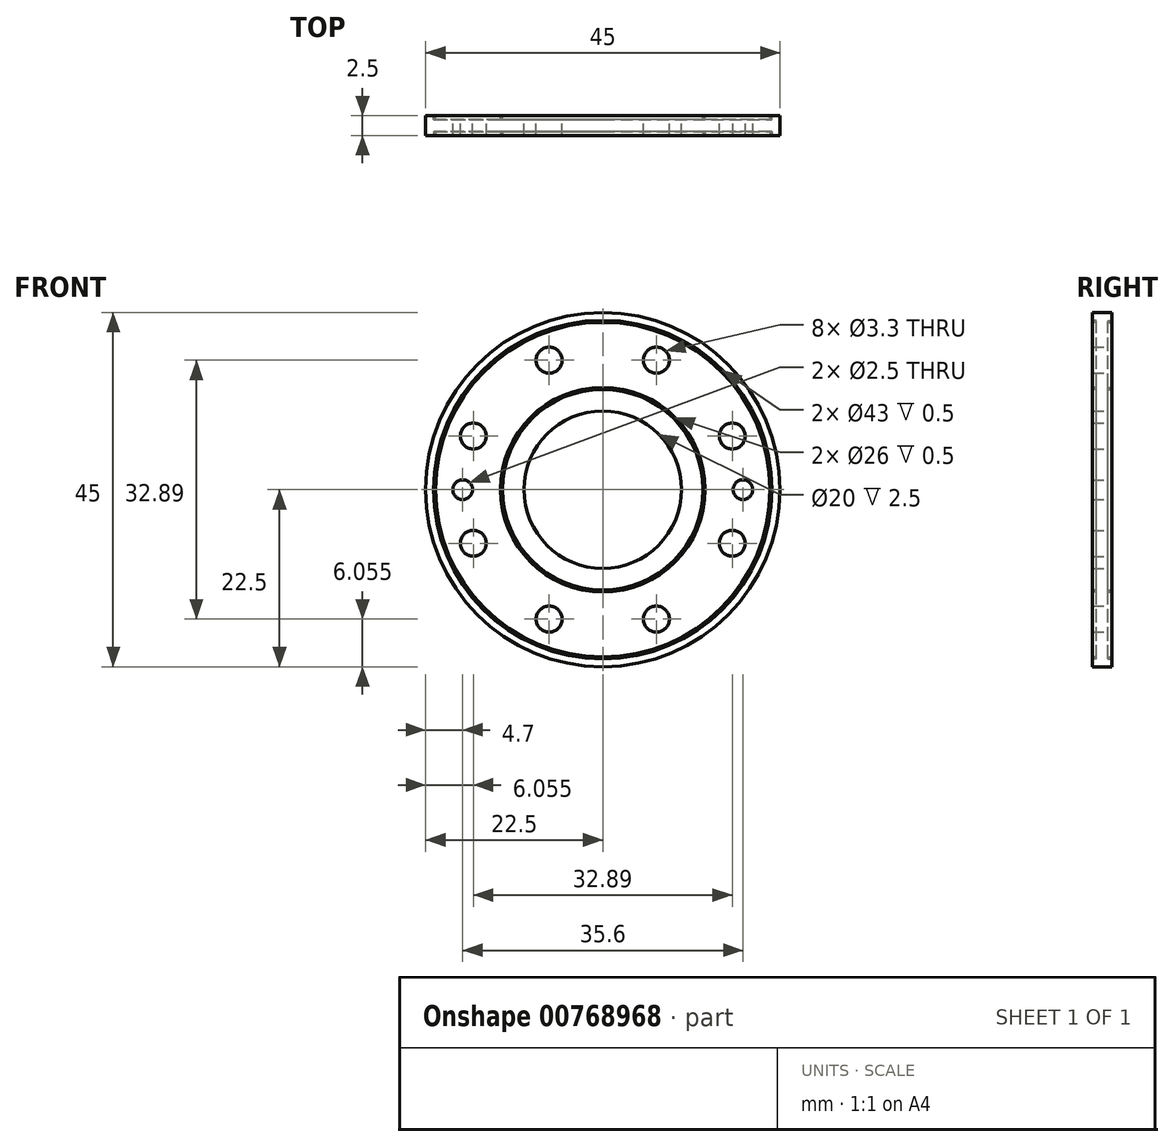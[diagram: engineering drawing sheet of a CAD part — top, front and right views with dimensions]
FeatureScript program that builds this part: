
annotation { "Feature Type Name" : "Feature", "Feature Type Description" : "" }
export const myFeature = defineFeature(function(context is Context, id is Id, definition is map)
    precondition{}
    {
        {
            var Q0;
            Q0=qCreatedBy(makeId("Front.planeOp"),FACE);
            var sketch = newSketch(context, id + "F0", { "sketchPlane" : qUnion([Q0])});
            skCircle(sketch, "E0", {"center": v(0, 0) * mm, "radius": 22.5 * mm});
            skCircle(sketch, "E1", {"center": v(0, 0) * mm, "radius": 10 * mm});
            skCircle(sketch, "E2", {"center": v(0, 0) * mm, "radius": 17.8 * mm, "construction": true});
            skLineSegment(sketch, "E3", {"start": v(0, 0) * mm, "end": v(-32.16, 13.32) * mm, "construction": true});
            skPoint(sketch, "E4", {"position": v(-16.45, 6.81) * mm});
            skPoint(sketch, "E5.1.0", {"position": v(-16.45, -6.81) * mm});
            skPoint(sketch, "E5.2.0", {"position": v(-6.81, -16.45) * mm});
            skPoint(sketch, "E5.3.0", {"position": v(6.81, -16.45) * mm});
            skPoint(sketch, "E5.4.0", {"position": v(16.45, -6.81) * mm});
            skPoint(sketch, "E5.5.0", {"position": v(16.45, 6.81) * mm});
            skPoint(sketch, "E5.6.0", {"position": v(6.81, 16.45) * mm});
            skPoint(sketch, "E5.7.0", {"position": v(-6.81, 16.45) * mm});
            skPoint(sketch, "E6", {"position": v(-17.8, 0) * mm});
            skPoint(sketch, "E7", {"position": v(17.8, 0) * mm});
            skSolve(sketch);
        }
        {
            var Q0;
            Q0=makeQuery(id+"F0.imprint","IMPRINT",FACE,{"disambiguationData":[TD([[makeQuery(id+"F0.imprint","IMPRINT",EDGE,{"derivedFrom":sQuery(id+"F0.wireOp",EDGE,"E0")}),1.0]])]});
            extrude(context, id + "F1", {"entities" : qUnion([Q0]), "depth" : 2.5 * mm, "offsetDistance" : 25 * mm});
        }
        {
            var Q0;
            Q0=sQuery(id+"F0.wireOp",VERTEX,"E4");
            var Q1;
            Q1=sQuery(id+"F0.wireOp",VERTEX,"E5.7.0");
            var Q2;
            Q2=sQuery(id+"F0.wireOp",VERTEX,"E5.6.0");
            var Q3;
            Q3=sQuery(id+"F0.wireOp",VERTEX,"E5.5.0");
            var Q4;
            Q4=sQuery(id+"F0.wireOp",VERTEX,"E5.4.0");
            var Q5;
            Q5=sQuery(id+"F0.wireOp",VERTEX,"E5.3.0");
            var Q6;
            Q6=sQuery(id+"F0.wireOp",VERTEX,"E5.2.0");
            var Q7;
            Q7=sQuery(id+"F0.wireOp",VERTEX,"E5.1.0");
            var Q8;
            Q8=makeQuery(id+"F1.opExtrude","SWEPT_BODY",BODY,{"disambiguationData":[OSD([sQuery(id+"F0.wireOp",EDGE,"E0"),sQuery(id+"F0.wireOp",EDGE,"E1")])]});
            hole(context, id + "F2", {"style" : HoleStyle.SIMPLE, "endStyle" : HoleEndStyle.THROUGH, "oppositeDirection" : true, "standardTappedOrClearance" : lookupTablePath({ "standard" : "ISO", "fit" : "Normal", "size" : "M3", "type" : "Clearance" }), "standardBlindInLast" : lookupTablePath({ "fit" : "Standard", "standard" : "ISO", "size" : "M3", "type" : "Clearance" }), "holeDiameter" : 3.3 * mm, "majorDiameter" : 5 * mm, "isTappedThrough" : true, "tappedDepth" : 12 * mm, "tapClearance" : 3, "locations" : qUnion([Q0, Q1, Q2, Q3, Q4, Q5, Q6, Q7]), "scope" : qUnion([Q8])});
        }
        {
            var Q0;
            Q0=sQuery(id+"F0.wireOp",VERTEX,"E6");
            var Q1;
            Q1=sQuery(id+"F0.wireOp",VERTEX,"E7");
            var Q2;
            Q2=makeQuery(id+"F1.opExtrude","SWEPT_BODY",BODY,{"disambiguationData":[OSD([sQuery(id+"F0.wireOp",EDGE,"E0"),sQuery(id+"F0.wireOp",EDGE,"E1")])]});
            hole(context, id + "F3", {"style" : HoleStyle.SIMPLE, "endStyle" : HoleEndStyle.THROUGH, "oppositeDirection" : true, "standardTappedOrClearance" : lookupTablePath({ "standard" : "ISO", "engagement" : "75%", "pitch" : "0.5 mm", "size" : "M3", "type" : "Tapped" }), "standardBlindInLast" : lookupTablePath({ "standard" : "ISO", "engagement" : "75%", "pitch" : "0.5 mm", "size" : "M3", "type" : "Tapped" }), "holeDiameter" : 2.5 * mm, "majorDiameter" : 3 * mm, "showTappedDepth" : true, "isTappedThrough" : true, "tappedDepth" : 12 * mm, "tapClearance" : 3, "locations" : qUnion([Q0, Q1]), "scope" : qUnion([Q2])});
        }
        {
            var Q0;
            Q0=makeQuery(id+"F1.opExtrude","CAP_FACE",FACE,{"disambiguationData":[OSD([sQuery(id+"F0.wireOp",EDGE,"E0"),sQuery(id+"F0.wireOp",EDGE,"E1")])],"isStart":false});
            var sketch = newSketch(context, id + "F4", { "sketchPlane" : qUnion([Q0])});
            skCircle(sketch, "E8", {"center": v(0, 0) * mm, "radius": 21.5 * mm});
            skCircle(sketch, "E9", {"center": v(0, 0) * mm, "radius": 21.25 * mm});
            skCircle(sketch, "E10", {"center": v(0, 0) * mm, "radius": 12.75 * mm});
            skCircle(sketch, "E11", {"center": v(0, 0) * mm, "radius": 13 * mm});
            skSolve(sketch);
        }
        {
            var Q0;
            Q0=makeQuery(id+"F4.imprint","IMPRINT",FACE,{"disambiguationData":[TD([[makeQuery(id+"F4.imprint","IMPRINT",EDGE,{"derivedFrom":sQuery(id+"F4.wireOp",EDGE,"E8")}),1.0]])]});
            var Q1;
            Q1=makeQuery(id+"F4.imprint","IMPRINT",FACE,{"disambiguationData":[TD([[makeQuery(id+"F4.imprint","IMPRINT",EDGE,{"derivedFrom":sQuery(id+"F4.wireOp",EDGE,"E10")}),-1.0]])]});
            extrude(context, id + "F5", {"entities" : qUnion([Q0, Q1]), "operationType" : NewBodyOperationType.REMOVE, "oppositeDirection" : true, "depth" : 0.5 * mm, "offsetDistance" : 25 * mm});
        }
        {
            var Q0;
            Q0=makeQuery(id+"F0.imprint","IMPRINT",FACE,{"disambiguationData":[TD([[makeQuery(id+"F0.imprint","IMPRINT",EDGE,{"derivedFrom":sQuery(id+"F0.wireOp",EDGE,"E0")}),1.0]])]});
            var sketch = newSketch(context, id + "F6", { "sketchPlane" : qUnion([Q0])});
            skCircle(sketch, "E12", {"center": v(0, 0) * mm, "radius": 21.5 * mm});
            skCircle(sketch, "E13", {"center": v(0, 0) * mm, "radius": 21.25 * mm});
            skCircle(sketch, "E14", {"center": v(0, 0) * mm, "radius": 13 * mm});
            skCircle(sketch, "E15", {"center": v(0, 0) * mm, "radius": 12.75 * mm});
            skSolve(sketch);
        }
        {
            var Q0;
            Q0=makeQuery(id+"F6.imprint","IMPRINT",FACE,{"disambiguationData":[TD([[makeQuery(id+"F6.imprint","IMPRINT",EDGE,{"derivedFrom":sQuery(id+"F6.wireOp",EDGE,"E12")}),1.0]])]});
            var Q1;
            Q1=makeQuery(id+"F6.imprint","IMPRINT",FACE,{"disambiguationData":[TD([[makeQuery(id+"F6.imprint","IMPRINT",EDGE,{"derivedFrom":sQuery(id+"F6.wireOp",EDGE,"E14")}),1.0]])]});
            extrude(context, id + "F7", {"entities" : qUnion([Q0, Q1]), "operationType" : NewBodyOperationType.REMOVE, "depth" : 0.5 * mm, "offsetDistance" : 25 * mm});
        }
    });
